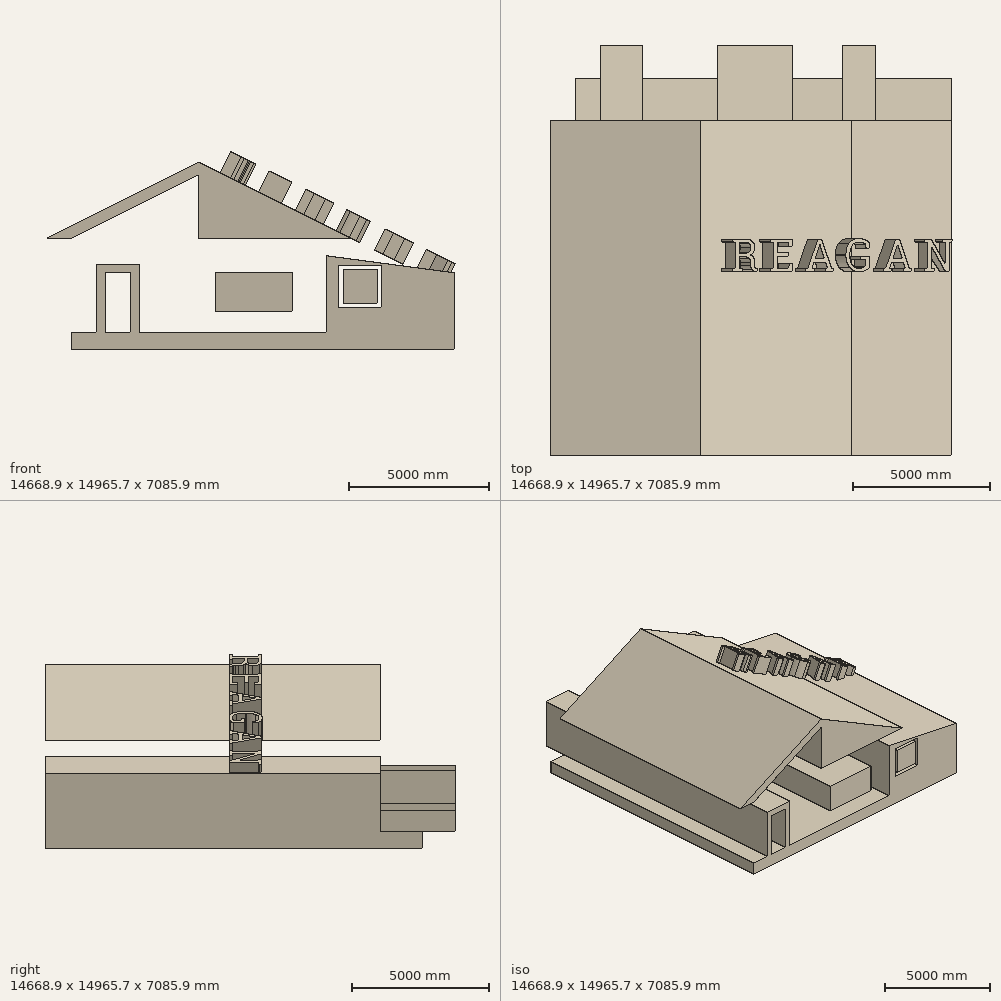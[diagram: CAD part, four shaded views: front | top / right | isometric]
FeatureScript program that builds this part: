
annotation { "Feature Type Name" : "Feature", "Feature Type Description" : "" }
export const myFeature = defineFeature(function(context is Context, id is Id, definition is map)
    precondition{}
    {
        {
            var Q0;
            Q0=qCreatedBy(makeId("Front.planeOp"),FACE);
            var sketch = newSketch(context, id + "F0", { "sketchPlane" : qUnion([Q0])});
            skLineSegment(sketch, "E0", {"start": v(0, 0) * mm, "end": v(-4572, 0) * mm});
            skLineSegment(sketch, "E1", {"start": v(-4572, 0) * mm, "end": v(0, 0) * mm});
            skLineSegment(sketch, "E2", {"start": v(4572, 0) * mm, "end": v(0, 0) * mm});
            skLineSegment(sketch, "E3", {"start": v(0, 0) * mm, "end": v(0, 2286) * mm});
            skLineSegment(sketch, "E4", {"start": v(0, 2286) * mm, "end": v(4572, 0) * mm});
            skLineSegment(sketch, "E5", {"start": v(0, 2286) * mm, "end": v(-4572, 0) * mm});
            skLineSegment(sketch, "E6", {"start": v(-4572, 0) * mm, "end": v(-5486.4, 0) * mm});
            skLineSegment(sketch, "E7", {"start": v(0, 2286) * mm, "end": v(0, 2743.2) * mm});
            skLineSegment(sketch, "E8", {"start": v(4572, 0) * mm, "end": v(5486.4, 0) * mm});
            skLineSegment(sketch, "E9", {"start": v(-5486.4, 0) * mm, "end": v(0, 2743.2) * mm});
            skLineSegment(sketch, "E10", {"start": v(0, 2743.2) * mm, "end": v(5486.4, 0) * mm});
            skLineSegment(sketch, "E11", {"start": v(-4572, 0) * mm, "end": v(-4572, -3352.8) * mm});
            skLineSegment(sketch, "E12", {"start": v(-4572, -3352.8) * mm, "end": v(4572, -3352.8) * mm});
            skLineSegment(sketch, "E13", {"start": v(4572, -3352.8) * mm, "end": v(4572, 0) * mm});
            skLineSegment(sketch, "E14", {"start": v(-4572, -3352.8) * mm, "end": v(-4572, -3962.4) * mm});
            skLineSegment(sketch, "E15", {"start": v(-4572, -3962.4) * mm, "end": v(4572, -3962.4) * mm});
            skLineSegment(sketch, "E16", {"start": v(4572, -3962.4) * mm, "end": v(4572, -3352.8) * mm});
            skLineSegment(sketch, "E17", {"start": v(609.6, -2590.8) * mm, "end": v(3352.8, -2590.8) * mm});
            skLineSegment(sketch, "E18", {"start": v(4572, -3962.4) * mm, "end": v(9144, -3962.4) * mm});
            skLineSegment(sketch, "E19", {"start": v(9144, -3962.4) * mm, "end": v(9144, -3352.8) * mm});
            skLineSegment(sketch, "E20", {"start": v(4572, -3352.8) * mm, "end": v(9144, -3352.8) * mm});
            skLineSegment(sketch, "E21", {"start": v(9144, -3352.8) * mm, "end": v(9144, -609.6) * mm});
            skLineSegment(sketch, "E22", {"start": v(4572, 0) * mm, "end": v(9144, -603.23) * mm});
            skLineSegment(sketch, "E23", {"start": v(4572, -609.6) * mm, "end": v(9144, -1219.2) * mm});
            skLineSegment(sketch, "E24", {"start": v(609.6, -2590.8) * mm, "end": v(609.6, -1219.2) * mm});
            skLineSegment(sketch, "E25", {"start": v(609.6, -1219.2) * mm, "end": v(3352.8, -1219.2) * mm});
            skLineSegment(sketch, "E26", {"start": v(3352.8, -2590.8) * mm, "end": v(3352.8, -1219.2) * mm});
            skLineSegment(sketch, "E27.bottom", {"start": v(-3352.8, -3352.8) * mm, "end": v(-2438.4, -3352.8) * mm});
            skLineSegment(sketch, "E27.left", {"start": v(-3352.8, -3352.8) * mm, "end": v(-3352.8, -1219.2) * mm});
            skLineSegment(sketch, "E27.right", {"start": v(-2438.4, -3352.8) * mm, "end": v(-2438.4, -1219.2) * mm});
            skLineSegment(sketch, "E28.0", {"start": v(457.2, -1066.8) * mm, "end": v(3505.2, -1066.8) * mm});
            skLineSegment(sketch, "E28.1", {"start": v(457.2, -2743.2) * mm, "end": v(457.2, -1066.8) * mm});
            skLineSegment(sketch, "E28.2", {"start": v(457.2, -2743.2) * mm, "end": v(3505.2, -2743.2) * mm});
            skLineSegment(sketch, "E28.3", {"start": v(3505.2, -2743.2) * mm, "end": v(3505.2, -1066.8) * mm});
            skLineSegment(sketch, "E29", {"start": v(-3352.8, -1219.2) * mm, "end": v(-2438.4, -1219.2) * mm});
            skLineSegment(sketch, "E30.0", {"start": v(-2133.6, -3352.8) * mm, "end": v(-2133.6, -914.4) * mm});
            skLineSegment(sketch, "E30.1", {"start": v(-3657.6, -914.4) * mm, "end": v(-2133.6, -914.4) * mm});
            skLineSegment(sketch, "E30.2", {"start": v(-3657.6, -3352.8) * mm, "end": v(-3657.6, -914.4) * mm});
            skLineSegment(sketch, "E31.bottom", {"start": v(5158.32, -1099.65) * mm, "end": v(6377.52, -1099.65) * mm});
            skLineSegment(sketch, "E31.top", {"start": v(5158.32, -2318.85) * mm, "end": v(6377.52, -2318.85) * mm});
            skLineSegment(sketch, "E31.left", {"start": v(5158.32, -1099.65) * mm, "end": v(5158.32, -2318.85) * mm});
            skLineSegment(sketch, "E31.right", {"start": v(6377.52, -1099.65) * mm, "end": v(6377.52, -2318.85) * mm});
            skLineSegment(sketch, "E32.0", {"start": v(5005.92, -947.25) * mm, "end": v(6529.92, -947.25) * mm});
            skLineSegment(sketch, "E32.1", {"start": v(5005.92, -947.25) * mm, "end": v(5005.92, -2471.25) * mm});
            skLineSegment(sketch, "E32.2", {"start": v(5005.92, -2471.25) * mm, "end": v(6529.92, -2471.25) * mm});
            skLineSegment(sketch, "E32.3", {"start": v(6529.92, -947.25) * mm, "end": v(6529.92, -2471.25) * mm});
            skSolve(sketch);
        }
        {
            var Q0;
            Q0=makeQuery(id+"F0.imprint","IMPRINT",FACE,{"disambiguationData":[TD([[makeQuery(id+"F0.imprint","IMPRINT",EDGE,{"derivedFrom":sQuery(id+"F0.wireOp",EDGE,"E5")}),-1.0]])]});
            var Q1;
            Q1=makeQuery(id+"F0.imprint","IMPRINT",FACE,{"disambiguationData":[TD([[makeQuery(id+"F0.imprint","IMPRINT",EDGE,{"derivedFrom":sQuery(id+"F0.wireOp",EDGE,"E4")}),1.0]])]});
            extrude(context, id + "F1", {"entities" : qUnion([Q0, Q1]), "depth" : 30.48 * mm, "offsetDistance" : 30.48 * mm, "hasSecondDirection" : true, "secondDirectionOppositeDirection" : true, "secondDirectionDepth" : 12192 * mm});
        }
        {
            var Q0;
            Q0=makeQuery(id+"F0.imprint","IMPRINT",FACE,{"disambiguationData":[TD([[makeQuery(id+"F0.imprint","IMPRINT",EDGE,{"derivedFrom":sQuery(id+"F0.wireOp",EDGE,"E1")}),1.0]])]});
            var Q1;
            Q1=makeQuery(id+"F0.imprint","IMPRINT",FACE,{"disambiguationData":[TD([[makeQuery(id+"F0.imprint","IMPRINT",EDGE,{"derivedFrom":sQuery(id+"F0.wireOp",EDGE,"E1")}),-1.0]])]});
            var Q2;
            Q2=makeQuery(id+"F0.imprint","IMPRINT",FACE,{"disambiguationData":[TD([[makeQuery(id+"F0.imprint","IMPRINT",EDGE,{"derivedFrom":sQuery(id+"F0.wireOp",EDGE,"E2")}),-1.0]])]});
            var Q3;
            {var subQ1=sQuery(id+"F0.wireOp",EDGE,"E20");Q3=makeQuery(id+"F0.imprint","IMPRINT",FACE,{"disambiguationData":[TD([[makeQuery(id+"F0.imprint","IMPRINT",EDGE,{"derivedFrom":subQ1}),1.0]])]});}
            extrude(context, id + "F2", {"entities" : qUnion([Q0, Q1, Q2, Q3]), "operationType" : NewBodyOperationType.ADD, "depth" : 30.48 * mm, "offsetDistance" : 30.48 * mm, "hasSecondDirection" : true, "secondDirectionOppositeDirection" : true, "secondDirectionDepth" : 12192 * mm});
        }
        {
            var Q0;
            {var subQ5=sQuery(id+"F0.wireOp",EDGE,"E14");Q0=makeQuery(id+"F0.imprint","IMPRINT",FACE,{"disambiguationData":[TD([[makeQuery(id+"F0.imprint","IMPRINT",EDGE,{"derivedFrom":subQ5}),1.0]])]});}
            var Q1;
            Q1=makeQuery(id+"F0.imprint","IMPRINT",FACE,{"disambiguationData":[TD([[makeQuery(id+"F0.imprint","IMPRINT",EDGE,{"derivedFrom":sQuery(id+"F0.wireOp",EDGE,"E16")}),-1.0]])]});
            extrude(context, id + "F3", {"entities" : qUnion([Q0, Q1]), "operationType" : NewBodyOperationType.ADD, "depth" : 30.48 * mm, "offsetDistance" : 30.48 * mm, "hasSecondDirection" : true, "secondDirectionOppositeDirection" : true, "secondDirectionDepth" : 13716 * mm});
        }
        {
            var Q0;
            {var subQ1=sQuery(id+"F0.wireOp",EDGE,"E27.left");Q0=makeQuery(id+"F0.imprint","IMPRINT",FACE,{"disambiguationData":[TD([[makeQuery(id+"F0.imprint","IMPRINT",EDGE,{"derivedFrom":subQ1}),1.0]])]});}
            var Q1;
            Q1=makeQuery(id+"F0.imprint","IMPRINT",FACE,{"disambiguationData":[TD([[makeQuery(id+"F0.imprint","IMPRINT",EDGE,{"derivedFrom":sQuery(id+"F0.wireOp",EDGE,"E27.bottom")}),1.0]])]});
            var Q2;
            Q2=makeQuery(id+"F0.imprint","IMPRINT",FACE,{"disambiguationData":[TD([[makeQuery(id+"F0.imprint","IMPRINT",EDGE,{"derivedFrom":sQuery(id+"F0.wireOp",EDGE,"E17")}),1.0]])]});
            var Q3;
            Q3=makeQuery(id+"F0.imprint","IMPRINT",FACE,{"disambiguationData":[TD([[makeQuery(id+"F0.imprint","IMPRINT",EDGE,{"derivedFrom":sQuery(id+"F0.wireOp",EDGE,"E31.bottom")}),-1.0]])]});
            extrude(context, id + "F4", {"entities" : qUnion([Q0, Q1, Q2, Q3]), "operationType" : NewBodyOperationType.ADD, "depth" : 30.48 * mm, "offsetDistance" : 30.48 * mm, "hasSecondDirection" : true, "secondDirectionOppositeDirection" : true, "secondDirectionDepth" : 14935.2 * mm});
        }
        {
            var Q0;
            Q0=sQuery(id+"F0.wireOp",EDGE,"E29");
            var Q1;
            Q1=sQuery(id+"F0.wireOp",EDGE,"E27.left");
            var Q2;
            Q2=sQuery(id+"F0.wireOp",EDGE,"E27.right");
            var Q3;
            Q3=sQuery(id+"F0.wireOp",EDGE,"E30.1");
            var Q4;
            Q4=sQuery(id+"F0.wireOp",EDGE,"E30.2");
            var Q5;
            Q5=sQuery(id+"F0.wireOp",EDGE,"E30.0");
            extrude(context, id + "F5", {"bodyType" : ToolBodyType.SURFACE, "surfaceEntities" : qUnion([Q0, Q1, Q2, Q3, Q4, Q5]), "depth" : 30.48 * mm, "offsetDistance" : 30.48 * mm, "hasSecondDirection" : true, "secondDirectionOppositeDirection" : true, "secondDirectionDepth" : 14935.2 * mm});
        }
        {
            var Q0;
            Q0=makeQuery(id+"F1.opExtrude","SWEPT_FACE",FACE,{"disambiguationData":[OSD([sQuery(id+"F0.wireOp",EDGE,"E10")])]});
            var sketch = newSketch(context, id + "F6", { "sketchPlane" : qUnion([Q0])});
            skText(sketch, "E33", { "text": "R E A G A N", "fontName": "RobotoSlab-Regular.ttf"});
            const initialGuessF6  = {"E33": [-0.42797, 6.68835, 1, 0, 1.19867]};
            skSetInitialGuess(sketch, initialGuessF6);
            skSolve(sketch);
        }
        {
            var Q0;
            Q0 = qSketchRegion(id + "F6", true);
            extrude(context, id + "F7", {"entities" : qUnion([Q0]), "operationType" : NewBodyOperationType.ADD, "depth" : 853.44 * mm, "offsetDistance" : 30.48 * mm});
        }
    });
